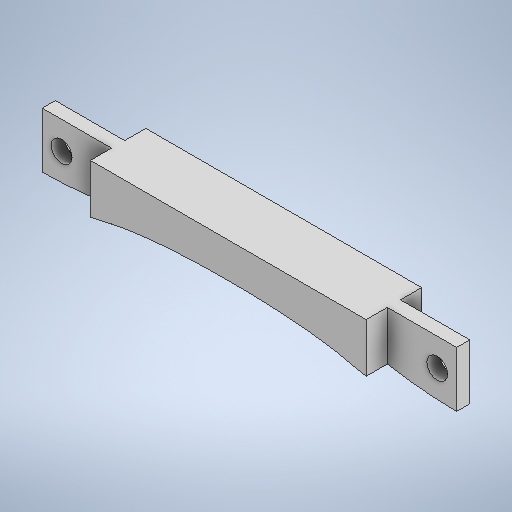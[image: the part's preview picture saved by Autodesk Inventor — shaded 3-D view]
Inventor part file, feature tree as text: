
AUTODESK INVENTOR PART (.ipt)
format: ipt  version: 2025.1 (Build 291241000, 241)  size: 269,824 bytes
history: native  units: in
note: dims shown in document units (in); Inventor stores cm internally (conversion verified against a paired STEP export)
features: sketch x3, extrude x3, fillet x1
ambient origin geometry x8: Origin, YZ Plane, XZ Plane, XY Plane, X Axis, Y Axis, Z Axis, Center Point
bodies: Solid1 (feature_tree)
feature tree (7):
  sketch  "Sketch1"  dims[d23=0.0591in d24=0.625in]
  extrude  "Extrusion1"  Depth=0.625in
  extrude  "Extrusion15"  Depth=2.4872in
  extrude  "Extrusion16"  Depth=0.5in TaperAngle=0.0deg
  fillet  "Fillet1"  Radius=0.45in
  sketch  "Sketch3"  dims[d25=0.1181in d27=2.4872in]
  sketch  "Sketch4"  dims[d81=0.5in d82=0.0in d109=0.8125in d110=0.0in d111=0.45in d112=0.188in d113=0.45in d114=0.188in d115=2.3125in d116=0.0in d117=0.5in d118=3.625in d28=0.0344in d29=0.5in d30=0.0344in]
